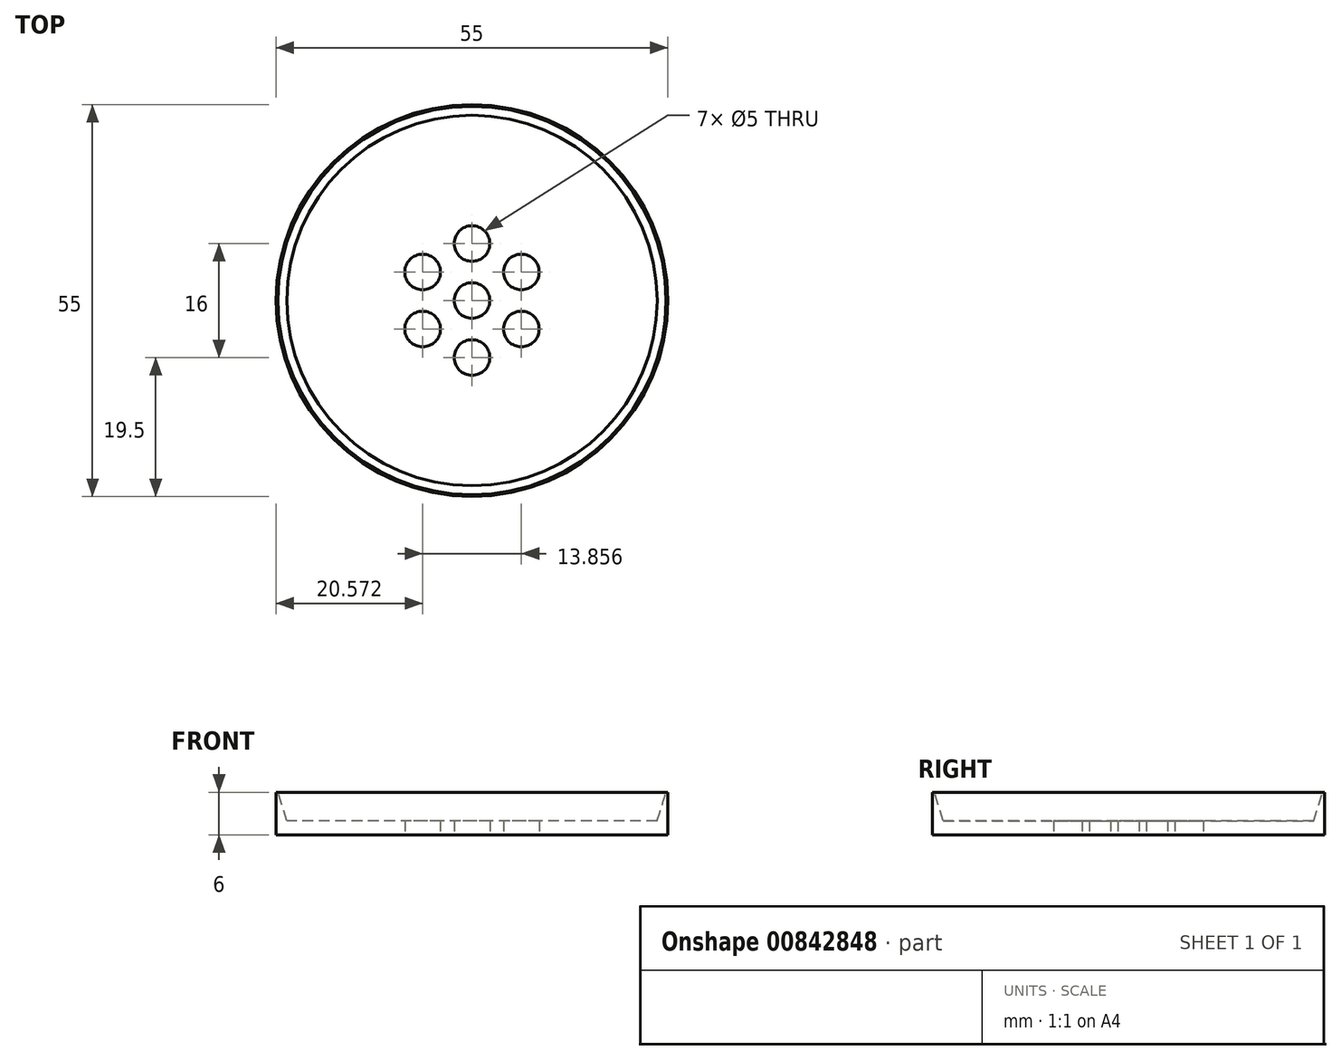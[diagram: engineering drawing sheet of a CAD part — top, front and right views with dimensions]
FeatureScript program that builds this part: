
annotation { "Feature Type Name" : "Feature", "Feature Type Description" : "" }
export const myFeature = defineFeature(function(context is Context, id is Id, definition is map)
    precondition{}
    {
        {
            var Q0;
            Q0=qCreatedBy(makeId("Top.planeOp"),FACE);
            var sketch = newSketch(context, id + "F0", { "sketchPlane" : qUnion([Q0])});
            skCircle(sketch, "E0", {"center": v(0, 0) * mm, "radius": 26 * mm});
            skCircle(sketch, "E1", {"center": v(0, 0) * mm, "radius": 27.5 * mm});
            skCircle(sketch, "E2", {"center": v(0, 8) * mm, "radius": 2.5 * mm});
            skCircle(sketch, "E3.1.0", {"center": v(-6.93, -4) * mm, "radius": 2.5 * mm});
            skCircle(sketch, "E3.2.0", {"center": v(6.93, -4) * mm, "radius": 2.5 * mm});
            skCircle(sketch, "E4", {"center": v(0, -8) * mm, "radius": 2.5 * mm});
            skCircle(sketch, "E5.1.0", {"center": v(6.93, 4) * mm, "radius": 2.5 * mm});
            skCircle(sketch, "E5.2.0", {"center": v(-6.93, 4) * mm, "radius": 2.5 * mm});
            skCircle(sketch, "E6", {"center": v(0, 0) * mm, "radius": 2.5 * mm});
            skCircle(sketch, "E7", {"center": v(0, 0) * mm, "radius": 12 * mm});
            skSolve(sketch);
        }
        {
            var Q0;
            Q0=makeQuery(id+"F0.imprint","IMPRINT",FACE,{"disambiguationData":[TD([[makeQuery(id+"F0.imprint","IMPRINT",EDGE,{"derivedFrom":sQuery(id+"F0.wireOp",EDGE,"E0")}),1.0]])]});
            var Q1;
            Q1=makeQuery(id+"F0.imprint","IMPRINT",FACE,{"disambiguationData":[TD([[makeQuery(id+"F0.imprint","IMPRINT",EDGE,{"derivedFrom":sQuery(id+"F0.wireOp",EDGE,"E2")}),-1.0]])]});
            extrude(context, id + "F1", {"entities" : qUnion([Q0, Q1]), "depth" : 2 * mm, "offsetDistance" : 25 * mm});
        }
        {
            var Q0;
            Q0=makeQuery(id+"F0.imprint","IMPRINT",FACE,{"disambiguationData":[TD([[makeQuery(id+"F0.imprint","IMPRINT",EDGE,{"derivedFrom":sQuery(id+"F0.wireOp",EDGE,"E0")}),-1.0]])]});
            extrude(context, id + "F2", {"entities" : qUnion([Q0]), "operationType" : NewBodyOperationType.ADD, "depth" : 6 * mm, "offsetDistance" : 25 * mm});
        }
        {
            var Q0;
            Q0=makeQuery(id+"F2.opExtrude","CAP_EDGE",EDGE,{"disambiguationData":[OSD([sQuery(id+"F0.wireOp",EDGE,"E0")])],"isStart":false});
            chamfer(context, id + "F3", {"entities" : qUnion([Q0]), "chamferType" : ChamferType.TWO_OFFSETS, "width1" : 4 * mm, "oppositeDirection" : false, "width2" : 1.25 * mm, "tangentPropagation" : true});
        }
    });
